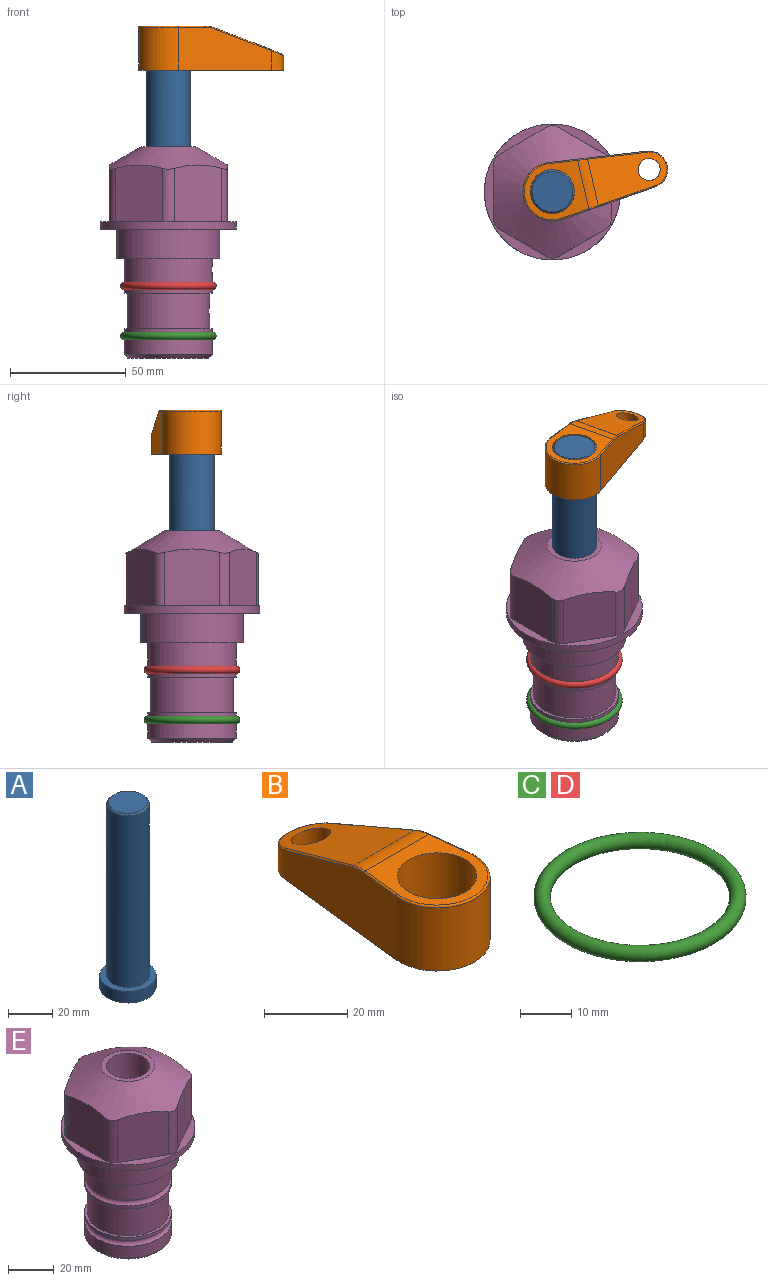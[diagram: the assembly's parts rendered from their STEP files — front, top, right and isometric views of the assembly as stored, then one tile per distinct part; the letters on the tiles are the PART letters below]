
ASSEMBLY  parts=5 mates=3
PART A: 6 faces, bbox 25.4x25.4x101.6 mm
  f0: plane 17.46x17.46mm, normal (0,0,1), area 239.5mm2, adj f5
  f1: plane 25.4x25.4mm, normal (0,0,-1), area 506.7mm2, adj f2
  f2: cylinder r=12.7mm len=25.4mm, axis (0,0,1), area 506.7mm2, adj f1,f3
  f3: plane 25.4x25.4mm, normal (0,0,1), area 221.7mm2, adj f2,f4
  f4: cylinder r=9.53mm len=94.46mm, axis (0,0,1), area 5653mm2, adj f3,f5
  f5: cone r=8.73mm half-angle=45deg, axis (0,0,-1), area 64.4mm2, adj f0,f4
PART B: 44 faces, bbox 27.5x64.5x19.1 mm
  f0: plane 2.3x0.95mm, normal (0,0,-1), area 1mm2, adj f25,f30,f34
  f1: plane 63.5x25.4mm, normal (0,0,-1), area 561.7mm2, adj f2,f3,f4,f5,f6,f7,f19,f20
  f2: cylinder r=12.7mm len=25.4mm, axis (0,0,-1), area 792.2mm2, adj f1,f3,f5,f13
  f3: plane 42.33x18.54mm, normal (0.99,0.11,0), area 647mm2, adj f1,f2,f4,f11,f12,f14
  f4: cylinder r=7.94mm len=15.78mm, axis (0,0,-1), area 158.6mm2, adj f1,f3,f5,f16
  f5: plane 42.33x18.54mm, normal (-0.99,0.11,0), area 647mm2, adj f1,f2,f4,f15,f17,f18
  f6: cylinder r=9.53mm len=19.05mm, axis (0,0,-1), area 1140.1mm2, adj f1,f8
  f7: cylinder r=4.76mm len=10.98mm, axis (0,0,-1), area 276.1mm2, adj f1,f9
  f8: plane 25.83x24.38mm, normal (0,0,1), area 262.2mm2, adj f6,f10,f11,f13,f15
  f9: plane 32.49x20.55mm, normal (0,0.34,0.94), area 489.9mm2, adj f7,f10,f14,f16,f18
  f10: cylinder r=12.7mm len=21.49mm, axis (-1,0,0), area 93.2mm2, adj f8,f9,f12,f17
  f11: cylinder r=0.51mm len=12.34mm, axis (0.11,-0.99,0), area 9.9mm2, adj f3,f8,f12,f13
  f12: bspline ~7.62x1.64mm, area 3.5mm2, adj f3,f10,f11,f14
  f13: torus R=12.19mm, axis (0,0,1), area 33.6mm2, adj f2,f8,f11,f15
  f14: cylinder r=0.51mm len=26.01mm, axis (0.1,-0.93,0.34), area 21.6mm2, adj f3,f9,f12,f16
  f15: cylinder r=0.51mm len=12.34mm, axis (0.11,0.99,0), area 9.9mm2, adj f5,f8,f13,f17
  f16: bspline ~15.78x7.05mm, area 15.7mm2, adj f4,f9,f14,f18
  f17: bspline ~7.62x1.64mm, area 3.5mm2, adj f5,f10,f15,f18
  f18: cylinder r=0.51mm len=26.01mm, axis (0.1,0.93,-0.34), area 21.6mm2, adj f5,f9,f16,f17
  f19: plane 21.6x14.29mm, normal (-0.99,-0.11,0), area 242.6mm2, adj f1,f26,f28,f34,f36,f38
  f20: plane 21.6x14.29mm, normal (0.99,-0.11,0), area 242.6mm2, adj f1,f27,f29,f37,f39,f41
  f21: cylinder r=12.7mm len=14.29mm, axis (0,0,-1), area 173.2mm2, adj f1,f26,f27,f30,f31,f33
  f22: cylinder r=7.94mm len=7.63mm, axis (0,0,-1), area 53.8mm2, adj f1,f28,f29,f42
  f23: plane 2.3x0.95mm, normal (0,0,-1), area 1mm2, adj f25,f33,f37
  f24: plane 17.94x12.32mm, normal (0,-0.34,-0.94), area 191.2mm2, adj f25,f38,f41,f42
  f25: cylinder r=9.53mm len=12.93mm, axis (-1,0,0), area 37.5mm2, adj f0,f23,f24,f31,f36,f39
  f26: cylinder r=1.59mm len=14.29mm, axis (0,0,-1), area 49mm2, adj f1,f19,f21,f32
  f27: cylinder r=1.59mm len=14.29mm, axis (0,0,-1), area 49mm2, adj f1,f20,f21,f35
  f28: cylinder r=1.59mm len=7.28mm, axis (0,0,-1), area 22.1mm2, adj f1,f19,f22,f40
  f29: cylinder r=1.59mm len=7.28mm, axis (0,0,-1), area 22.1mm2, adj f1,f20,f22,f43
  f30: torus R=14.29mm, axis (0,0,1), area 5.8mm2, adj f0,f21,f31,f32
  f31: bspline ~11.06x2.73mm, area 20.8mm2, adj f21,f25,f30,f33
  f32: sphere r=1.59mm, area 5.4mm2, adj f26,f30,f34
  f33: torus R=14.29mm, axis (0,0,1), area 5.8mm2, adj f21,f23,f31,f35
  f34: cylinder r=1.59mm len=1.68mm, axis (-0.11,0.99,0), area 2.4mm2, adj f0,f19,f32,f36
  f35: sphere r=1.59mm, area 5.4mm2, adj f27,f33,f37
  f36: bspline ~5.82x2.33mm, area 7.7mm2, adj f19,f25,f34,f38
  f37: cylinder r=1.59mm len=1.68mm, axis (0.11,0.99,0), area 2.4mm2, adj f20,f23,f35,f39
  f38: cylinder r=1.59mm len=18.33mm, axis (0.1,-0.93,0.34), area 46.7mm2, adj f19,f24,f36,f40
  f39: bspline ~5.82x2.33mm, area 7.7mm2, adj f20,f25,f37,f41
  f40: sphere r=1.59mm, area 3.6mm2, adj f28,f38,f42
  f41: cylinder r=1.59mm len=18.33mm, axis (0.1,0.93,-0.34), area 46.7mm2, adj f20,f24,f39,f43
  f42: bspline ~8.31x1.84mm, area 15.3mm2, adj f22,f24,f40,f43
  f43: sphere r=1.59mm, area 3.6mm2, adj f29,f41,f42
PART C: 1 faces, bbox 44.7x44.7x3.2 mm
  f0: torus R=19.05mm, axis (0,0,1), area 1193.9mm2
PART D: same geometry as C
PART E: 36 faces, bbox 58.7x58.7x91.2 mm
  f0: cylinder r=17.78mm len=35.56mm, axis (0,0,1), area 1670.8mm2, adj f23,f24,f31
  f1: cylinder r=19.05mm len=38.1mm, axis (0,0,1), area 1191.9mm2, adj f26,f27,f30
  f2: plane 58.66x58.66mm, normal (0,0,-1), area 1150.6mm2, adj f3,f28
  f3: cylinder r=29.33mm len=58.66mm, axis (0,0,-1), area 585.1mm2, adj f2,f4
  f4: plane 58.66x58.66mm, normal (0,0,1), area 475.9mm2, adj f3,f5,f6,f7,f8,f9,f10,f11
  f5: plane 24.5x20.32mm, normal (-0.5,0.87,0), area 562.8mm2, adj f4,f15,f16,f17
  f6: plane 24.5x20.32mm, normal (0.5,0.87,0), area 562.8mm2, adj f4,f14,f15,f17
  f7: plane 24.5x23.48mm, normal (1,0,0), area 562.8mm2, adj f4,f13,f14,f17
  f8: plane 24.5x20.32mm, normal (0.5,-0.87,0), area 562.8mm2, adj f4,f12,f13,f17
  f9: plane 24.5x20.32mm, normal (-0.5,-0.87,0), area 562.8mm2, adj f4,f11,f12,f17
  f10: plane 24.5x23.48mm, normal (-1,0,0), area 562.8mm2, adj f4,f11,f16,f17
  f11: cylinder r=5.08mm len=23.01mm, axis (0,0,-1), area 121.2mm2, adj f4,f9,f10,f17
  f12: cylinder r=5.08mm len=23.01mm, axis (0,0,-1), area 121.2mm2, adj f4,f8,f9,f17
  f13: cylinder r=5.08mm len=23.01mm, axis (0,0,-1), area 121.2mm2, adj f4,f7,f8,f17
  f14: cylinder r=5.08mm len=23.01mm, axis (0,0,-1), area 121.2mm2, adj f4,f6,f7,f17
  f15: cylinder r=5.08mm len=23.01mm, axis (0,0,-1), area 121.2mm2, adj f4,f5,f6,f17
  f16: cylinder r=5.08mm len=23.01mm, axis (0,0,-1), area 121.2mm2, adj f4,f5,f10,f17
  f17: cone r=11.73mm half-angle=60deg, axis (0,0,-1), area 2071.8mm2, adj f5,f6,f7,f8,f9,f10,f11,f12
  f18: plane 23.46x23.46mm, normal (0,0,1), area 147.4mm2, adj f17,f35
  f19: plane 34.93x34.93mm, normal (0,0,-1), area 958mm2, adj f29
  f20: cylinder r=19.05mm len=38.1mm, axis (0,0,1), area 760.1mm2, adj f21,f29
  f21: torus R=19.05mm, axis (0,0,1), area 565.3mm2, adj f20,f22
  f22: cylinder r=19.05mm len=38.1mm, axis (0,0,1), area 190mm2, adj f21,f23
  f23: plane 38.1x38.1mm, normal (0,0,1), area 146.9mm2, adj f0,f22
  f24: plane 38.1x38.1mm, normal (0,0,-1), area 146.9mm2, adj f0,f25
  f25: cylinder r=19.05mm len=38.1mm, axis (0,0,1), area 190mm2, adj f24,f26
  f26: torus R=19.05mm, axis (0,0,1), area 565.3mm2, adj f1,f25
  f27: plane 44.45x44.45mm, normal (0,0,-1), area 411.7mm2, adj f1,f28
  f28: cylinder r=22.23mm len=44.45mm, axis (0,0,1), area 1773.5mm2, adj f2,f27
  f29: cone r=19.05mm half-angle=45deg, axis (0,0,1), area 257.5mm2, adj f19,f20
  f30: cylinder r=3.17mm len=6.75mm, axis (-1,0,0), area 128mm2, adj f1,f33
  f31: cylinder r=3.17mm len=6.35mm, axis (-1,0,0), area 102.5mm2, adj f0,f33
  f32: plane 25.4x25.4mm, normal (0,0,1), area 506.7mm2, adj f33
  f33: cylinder r=12.7mm len=66.42mm, axis (0,0,-1), area 5236.2mm2, adj f30,f31,f32,f34
  f34: cone r=9.53mm half-angle=30deg, axis (0,0,-1), area 443.4mm2, adj f33,f35
  f35: cylinder r=9.53mm len=19.05mm, axis (0,0,-1), area 849mm2, adj f18,f34
PLACE A rot(axis=(0,0,1),12.9deg) t=(0,0,13.95)mm
PLACE B rot(axis=(0,0,-1),77.1deg) t=(0,0,68.56)mm
PLACE C t=(0,0,-21.59)mm
PLACE D at identity
PLACE E at identity fixed
MATE fastened C.f0 <-> E.f0  axis (0,0,1) through (0,0,-46.1)mm
MATE cylindrical A.f2 <-> E.f0  axis (0,0,1) through (0,0,39.59)mm
MATE fastened B.f2 <-> A.f2  axis (0,0,1) through (0,0,87.61)mm
